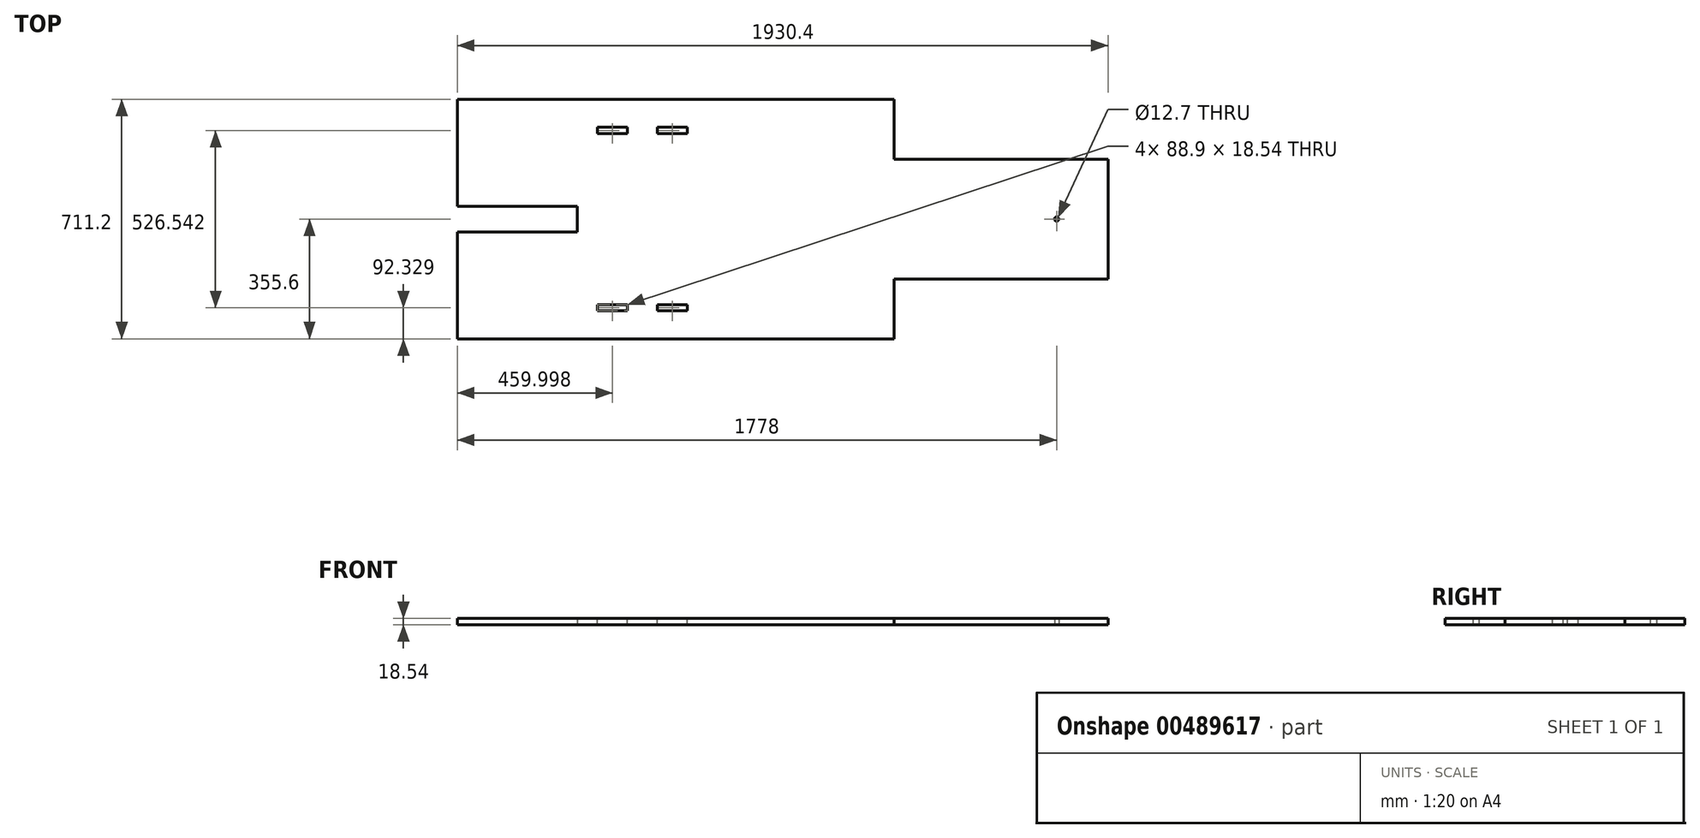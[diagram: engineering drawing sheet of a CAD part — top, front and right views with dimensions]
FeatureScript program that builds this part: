
annotation { "Feature Type Name" : "Feature", "Feature Type Description" : "" }
export const myFeature = defineFeature(function(context is Context, id is Id, definition is map)
    precondition{}
    {
        {
            var Q0;
            Q0=qCreatedBy(makeId("Top.planeOp"),FACE);
            var sketch = newSketch(context, id + "F0", { "sketchPlane" : qUnion([Q0])});
            skLineSegment(sketch, "E0.bottom", {"start": v(-954.26, 177.8) * mm, "end": v(341.14, 177.8) * mm});
            skLineSegment(sketch, "E0.top", {"start": v(-954.26, -533.4) * mm, "end": v(341.14, -533.4) * mm});
            skLineSegment(sketch, "E0.left", {"start": v(-954.26, 177.8) * mm, "end": v(-954.26, -139.7) * mm});
            skLineSegment(sketch, "E0.right", {"start": v(976.14, 0) * mm, "end": v(976.14, -355.6) * mm});
            skPoint(sketch, "E1", {"position": v(976.14, 177.8) * mm});
            skLineSegment(sketch, "E2", {"start": v(341.14, 177.8) * mm, "end": v(341.14, 0) * mm});
            skLineSegment(sketch, "E3", {"start": v(341.14, 0) * mm, "end": v(976.14, 0) * mm});
            skPoint(sketch, "E4.startSnap0", {"position": v(341.14, 88.9) * mm});
            skLineSegment(sketch, "E5", {"start": v(341.14, -533.4) * mm, "end": v(341.14, -355.6) * mm});
            skLineSegment(sketch, "E6", {"start": v(341.14, -355.6) * mm, "end": v(976.14, -355.6) * mm});
            skLineSegment(sketch, "E7", {"start": v(-954.26, -533.4) * mm, "end": v(-954.26, -215.9) * mm, "construction": true});
            skLineSegment(sketch, "E8", {"start": v(-954.26, -139.7) * mm, "end": v(-598.66, -139.7) * mm});
            skLineSegment(sketch, "E9", {"start": v(-954.26, -215.9) * mm, "end": v(-598.66, -215.9) * mm});
            skLineSegment(sketch, "E10", {"start": v(-598.66, -139.7) * mm, "end": v(-598.66, -215.9) * mm});
            skLineSegment(sketch, "E11", {"start": v(976.14, 0) * mm, "end": v(976.14, -177.8) * mm, "construction": true});
            skLineSegment(sketch, "E12", {"start": v(976.14, -177.8) * mm, "end": v(823.74, -177.8) * mm, "construction": true});
            skCircle(sketch, "E13", {"center": v(823.74, -177.8) * mm, "radius": 6.35 * mm});
            skLineSegment(sketch, "E14.trimOffspring", {"start": v(-954.26, -215.9) * mm, "end": v(-954.26, -533.4) * mm});
            skPoint(sketch, "E15.orphan", {"position": v(976.14, -533.4) * mm});
            skSolve(sketch);
        }
        {
            var Q0;
            Q0=makeQuery(id+"F0.imprint","IMPRINT",FACE,{"disambiguationData":[TD([[makeQuery(id+"F0.imprint","IMPRINT",EDGE,{"derivedFrom":sQuery(id+"F0.wireOp",EDGE,"E0.bottom")}),-1.0]])]});
            extrude(context, id + "F1", {"entities" : qUnion([Q0]), "depth" : 18.54 * mm, "offsetDistance" : 25.4 * mm});
        }
        {
            var Q0;
            Q0=makeQuery(id+"F1.opExtrude","CAP_FACE",FACE,{"disambiguationData":[OSD([sQuery(id+"F0.wireOp",EDGE,"E0.bottom"),sQuery(id+"F0.wireOp",EDGE,"E0.top"),sQuery(id+"F0.wireOp",EDGE,"E0.right"),sQuery(id+"F0.wireOp",EDGE,"E2"),sQuery(id+"F0.wireOp",EDGE,"E3"),sQuery(id+"F0.wireOp",EDGE,"E5"),sQuery(id+"F0.wireOp",EDGE,"E6"),sQuery(id+"F0.wireOp",EDGE,"E0.left"),sQuery(id+"F0.wireOp",EDGE,"E8"),sQuery(id+"F0.wireOp",EDGE,"E9"),sQuery(id+"F0.wireOp",EDGE,"E10"),sQuery(id+"F0.wireOp",EDGE,"E13"),sQuery(id+"F0.wireOp",EDGE,"E14.trimOffspring")])],"isStart":false});
            var sketch = newSketch(context, id + "F2", { "sketchPlane" : qUnion([Q0])});
            skLineSegment(sketch, "E16.bottom", {"start": v(-538.71, -431.8) * mm, "end": v(-449.81, -431.8) * mm});
            skLineSegment(sketch, "E16.top", {"start": v(-538.71, -450.34) * mm, "end": v(-449.81, -450.34) * mm});
            skLineSegment(sketch, "E16.left", {"start": v(-538.71, -431.8) * mm, "end": v(-538.71, -450.34) * mm});
            skLineSegment(sketch, "E16.right", {"start": v(-449.81, -431.8) * mm, "end": v(-449.81, -450.34) * mm});
            skLineSegment(sketch, "E17.bottom", {"start": v(-538.71, 94.74) * mm, "end": v(-449.81, 94.74) * mm});
            skLineSegment(sketch, "E17.top", {"start": v(-538.71, 76.2) * mm, "end": v(-449.81, 76.2) * mm});
            skLineSegment(sketch, "E17.left", {"start": v(-538.71, 94.74) * mm, "end": v(-538.71, 76.2) * mm});
            skLineSegment(sketch, "E17.right", {"start": v(-449.81, 94.74) * mm, "end": v(-449.81, 76.2) * mm});
            skPoint(sketch, "E18", {"position": v(-360.91, -431.8) * mm});
            skLineSegment(sketch, "E19", {"start": v(-360.91, -431.8) * mm, "end": v(-360.91, -450.34) * mm});
            skLineSegment(sketch, "E20", {"start": v(-360.91, -450.34) * mm, "end": v(-272.01, -450.34) * mm});
            skLineSegment(sketch, "E21", {"start": v(-272.01, -450.34) * mm, "end": v(-272.01, -431.8) * mm});
            skLineSegment(sketch, "E22", {"start": v(-272.01, -431.8) * mm, "end": v(-360.91, -431.8) * mm});
            skPoint(sketch, "E23", {"position": v(-360.91, 76.2) * mm});
            skLineSegment(sketch, "E24", {"start": v(-360.91, 76.2) * mm, "end": v(-360.91, 94.74) * mm});
            skLineSegment(sketch, "E25", {"start": v(-360.91, 94.74) * mm, "end": v(-272.01, 94.74) * mm});
            skLineSegment(sketch, "E26", {"start": v(-272.01, 94.74) * mm, "end": v(-272.01, 76.2) * mm});
            skLineSegment(sketch, "E27", {"start": v(-272.01, 76.2) * mm, "end": v(-360.91, 76.2) * mm});
            skSolve(sketch);
        }
        {
            var Q0;
            Q0 = qSketchRegion(id + "F2", true);
            extrude(context, id + "F3", {"entities" : qUnion([Q0]), "operationType" : NewBodyOperationType.REMOVE, "oppositeDirection" : true, "depth" : 25.4 * mm, "offsetDistance" : 25.4 * mm});
        }
    });
